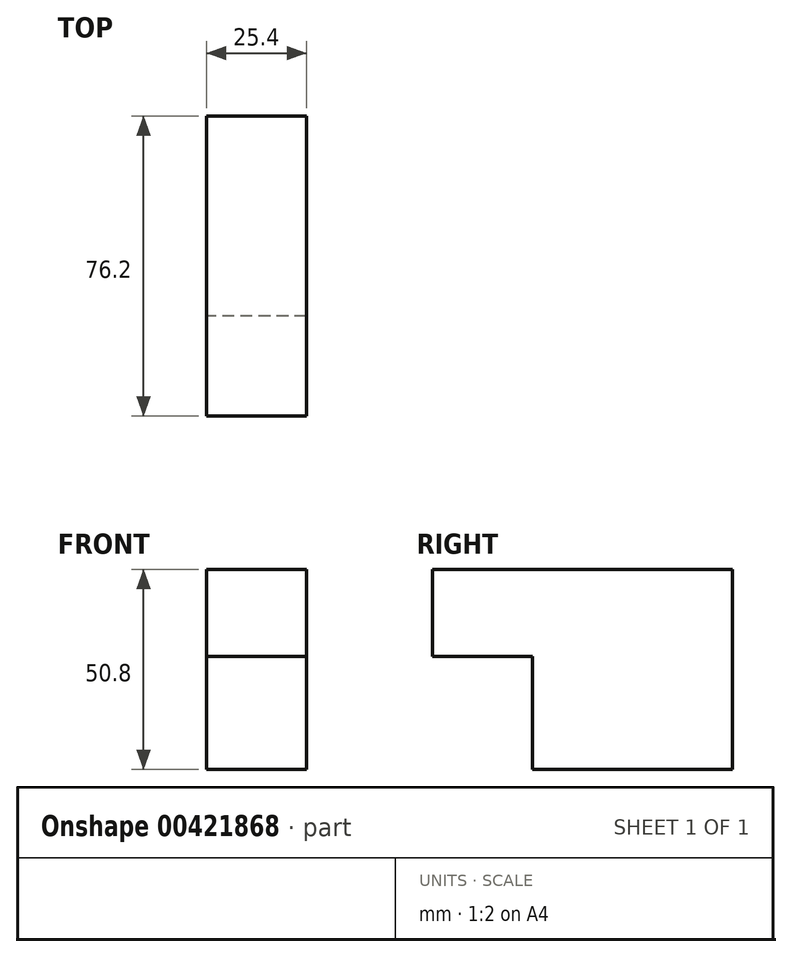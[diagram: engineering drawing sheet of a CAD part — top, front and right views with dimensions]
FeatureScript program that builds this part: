
annotation { "Feature Type Name" : "Feature", "Feature Type Description" : "" }
export const myFeature = defineFeature(function(context is Context, id is Id, definition is map)
    precondition{}
    {
        {
            var Q0;
            Q0=qCreatedBy(makeId("Front.planeOp"),FACE);
            var sketch = newSketch(context, id + "F0", { "sketchPlane" : qUnion([Q0])});
            skLineSegment(sketch, "E0", {"start": v(0, 0) * mm, "end": v(25.4, 0) * mm});
            skLineSegment(sketch, "E1", {"start": v(25.4, 0) * mm, "end": v(25.4, -50.8) * mm});
            skLineSegment(sketch, "E2", {"start": v(25.4, -50.8) * mm, "end": v(0, -50.8) * mm});
            skLineSegment(sketch, "E3", {"start": v(0, -50.8) * mm, "end": v(0, 0) * mm});
            skLineSegment(sketch, "E4", {"start": v(0, 0) * mm, "end": v(0, -50.8) * mm});
            skSolve(sketch);
        }
        {
            var Q0;
            Q0 = qSketchRegion(id + "F0", true);
            extrude(context, id + "F1", {"entities" : qUnion([Q0]), "depth" : 50.8 * mm});
        }
        {
            var Q0;
            Q0=makeQuery(id+"F1.opExtrude","CAP_FACE",FACE,{"disambiguationData":[OSD([sQuery(id+"F0.wireOp",EDGE,"E0"),sQuery(id+"F0.wireOp",EDGE,"E1"),sQuery(id+"F0.wireOp",EDGE,"E2"),sQuery(id+"F0.wireOp",EDGE,"E4")])],"isStart":false});
            var sketch = newSketch(context, id + "F2", { "sketchPlane" : qUnion([Q0])});
            skLineSegment(sketch, "E5.bottom", {"start": v(0, 0) * mm, "end": v(25.4, 0) * mm});
            skLineSegment(sketch, "E5.top", {"start": v(0, -22.13) * mm, "end": v(25.4, -22.13) * mm});
            skLineSegment(sketch, "E5.left", {"start": v(0, 0) * mm, "end": v(0, -22.13) * mm});
            skLineSegment(sketch, "E5.right", {"start": v(25.4, 0) * mm, "end": v(25.4, -22.13) * mm});
            skSolve(sketch);
        }
        {
            var Q0;
            Q0=makeQuery(id+"F2.imprint","IMPRINT",FACE,{"disambiguationData":[TD([[makeQuery(id+"F2.imprint","IMPRINT",EDGE,{"derivedFrom":sQuery(id+"F2.wireOp",EDGE,"E5.bottom")}),-1.0]])]});
            extrude(context, id + "F3", {"entities" : qUnion([Q0]), "operationType" : NewBodyOperationType.ADD, "depth" : 25.4 * mm});
        }
    });
